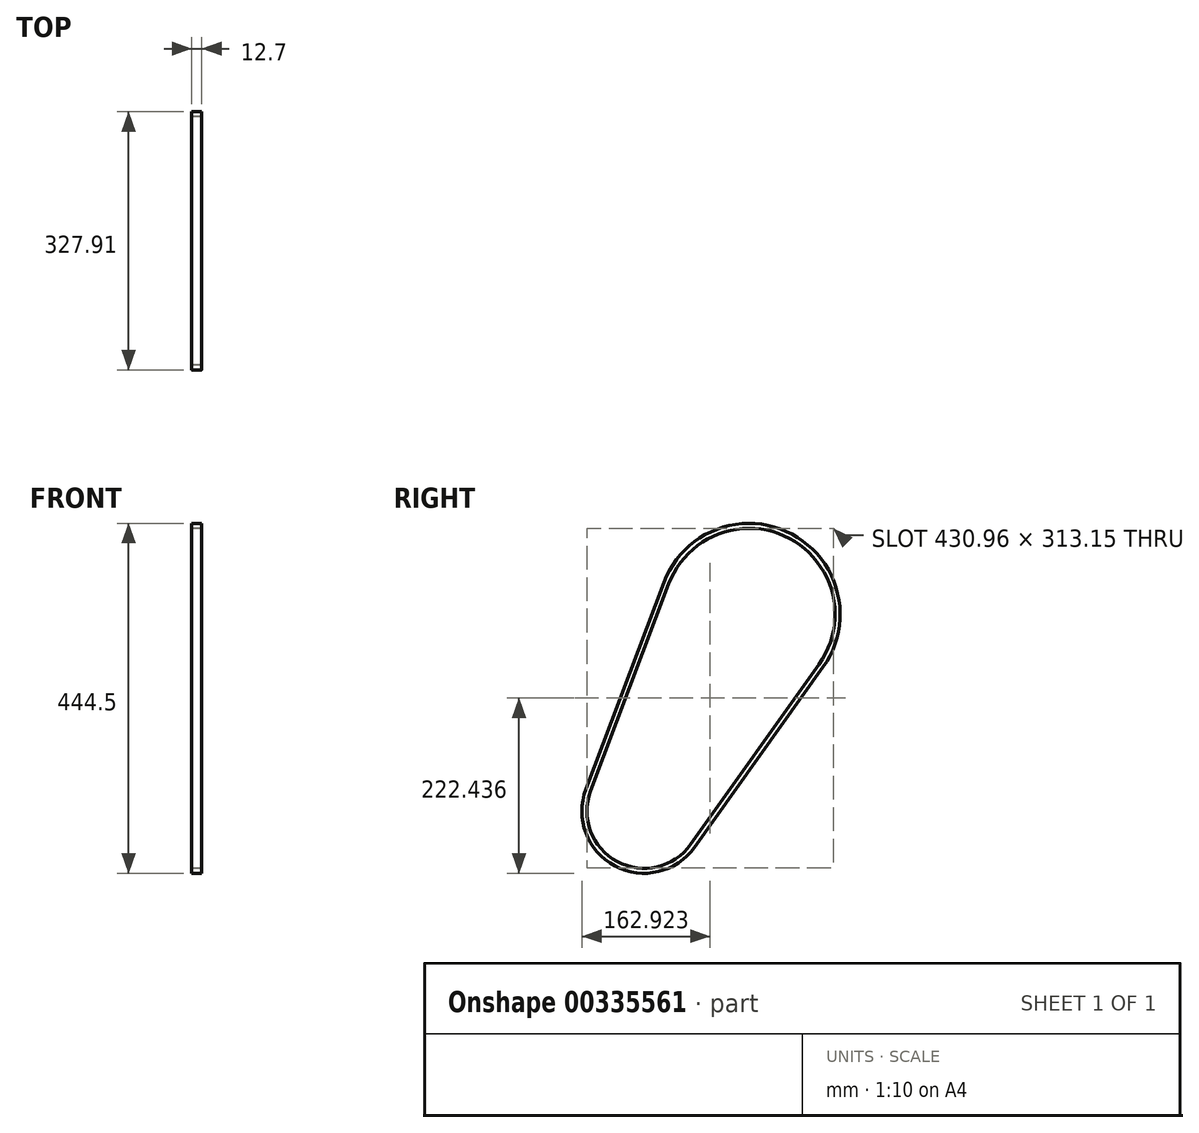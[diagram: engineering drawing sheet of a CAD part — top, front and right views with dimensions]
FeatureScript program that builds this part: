
annotation { "Feature Type Name" : "Feature", "Feature Type Description" : "" }
export const myFeature = defineFeature(function(context is Context, id is Id, definition is map)
    precondition{}
    {
        {
            var Q0;
            Q0=qCreatedBy(makeId("Right.planeOp"),FACE);
            var sketch = newSketch(context, id + "F0", { "sketchPlane" : qUnion([Q0])});
            skLineSegment(sketch, "E0", {"start": v(0, 0) * mm, "end": v(133.35, 0) * mm, "construction": true});
            skLineSegment(sketch, "E1", {"start": v(133.35, 0) * mm, "end": v(133.35, 249.94) * mm, "construction": true});
            skArc(sketch, "E2", {"start": v(-67.97, 25.63) * mm, "mid": v(-34.2, -64.1) * mm, "end": v(59.14, -42.18) * mm});
            skArc(sketch, "E3", {"start": v(222.27, 186.51) * mm, "mid": v(184.76, 346.3) * mm, "end": v(31.16, 288.48) * mm});
            skLineSegment(sketch, "E4", {"start": v(31.16, 288.48) * mm, "end": v(-67.97, 25.63) * mm});
            skLineSegment(sketch, "E5", {"start": v(222.27, 186.51) * mm, "end": v(59.14, -42.18) * mm});
            skLineSegment(sketch, "E6.0", {"start": v(25.21, 290.72) * mm, "end": v(-73.91, 27.87) * mm});
            skArc(sketch, "E6.1", {"start": v(227.44, 182.82) * mm, "mid": v(187.75, 351.9) * mm, "end": v(25.21, 290.72) * mm});
            skLineSegment(sketch, "E6.2", {"start": v(227.44, 182.82) * mm, "end": v(64.31, -45.87) * mm});
            skArc(sketch, "E6.3", {"start": v(-73.91, 27.87) * mm, "mid": v(-37.18, -69.7) * mm, "end": v(64.31, -45.87) * mm});
            skSolve(sketch);
        }
        {
            var Q0;
            Q0 = qSketchRegion(id + "F0", true);
            extrude(context, id + "F1", {"entities" : qUnion([Q0]), "endBound" : BoundingType.SYMMETRIC, "depth" : 12.7 * mm});
        }
    });
